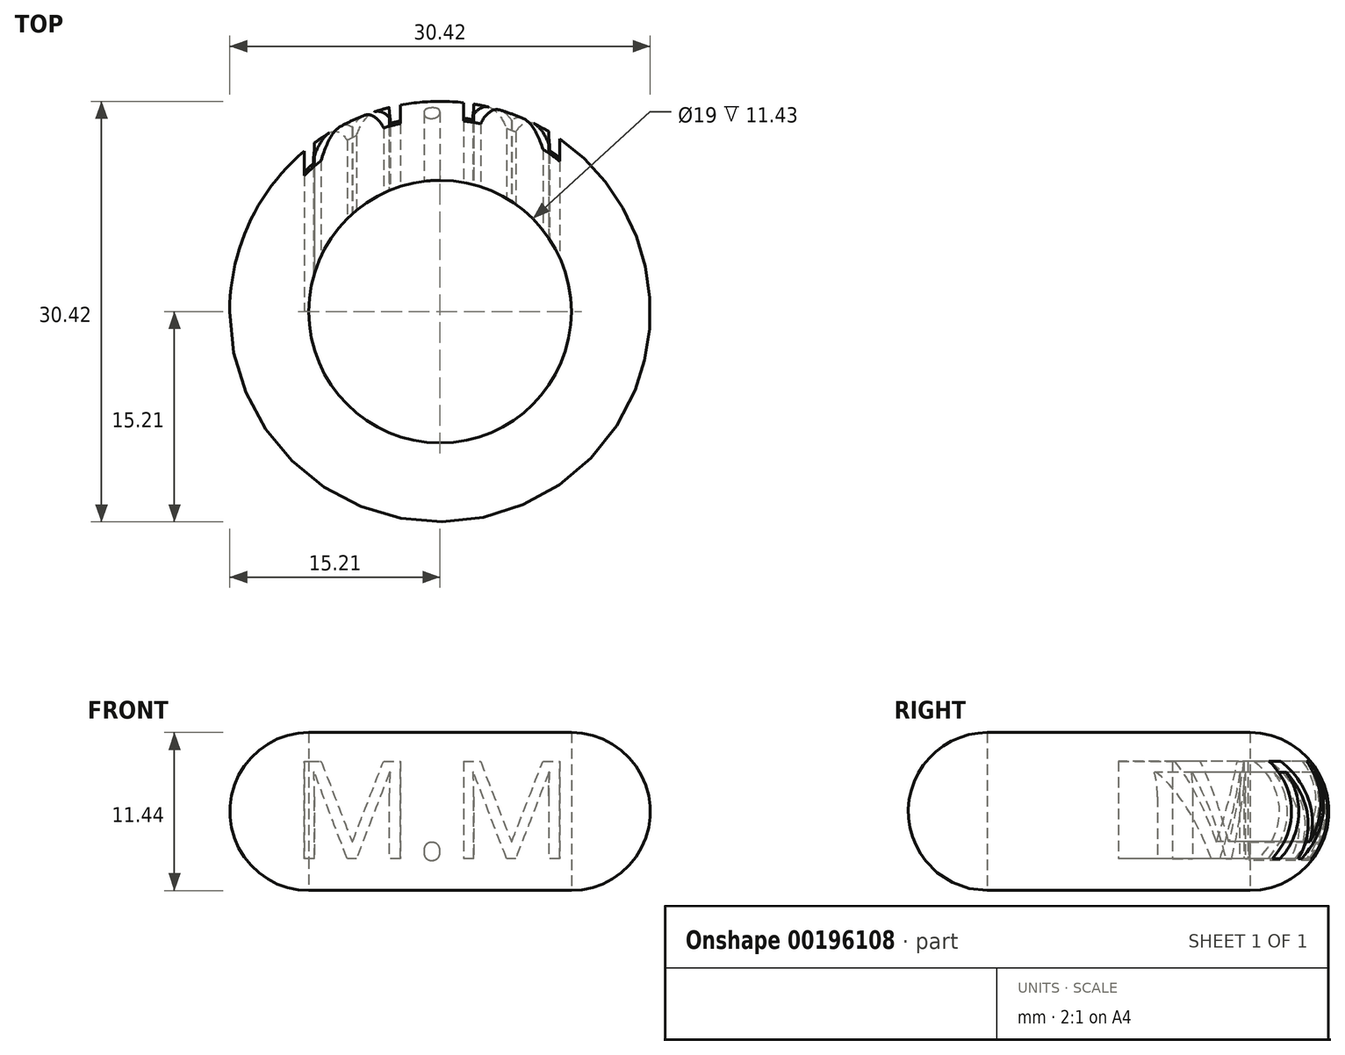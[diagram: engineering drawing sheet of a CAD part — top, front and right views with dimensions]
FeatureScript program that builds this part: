
annotation { "Feature Type Name" : "Feature", "Feature Type Description" : "" }
export const myFeature = defineFeature(function(context is Context, id is Id, definition is map)
    precondition{}
    {
        {
            var Q0;
            Q0=qCreatedBy(makeId("Front.planeOp"),FACE);
            var sketch = newSketch(context, id + "F0", { "sketchPlane" : qUnion([Q0])});
            skArc(sketch, "E0", {"start": v(9.5, -5.72) * mm, "mid": v(15.21, 0) * mm, "end": v(9.5, 5.72) * mm});
            skLineSegment(sketch, "E1", {"start": v(0, 0) * mm, "end": v(0, 10.97) * mm});
            skLineSegment(sketch, "E2", {"start": v(9.5, -5.72) * mm, "end": v(9.5, 5.72) * mm});
            skSolve(sketch);
        }
        {
            var Q0;
            Q0=makeQuery(id+"F0.imprint","IMPRINT",FACE,{"disambiguationData":[TD([[makeQuery(id+"F0.imprint","IMPRINT",EDGE,{"derivedFrom":sQuery(id+"F0.wireOp",EDGE,"E0")}),1.0]])]});
            var Q1;
            Q1=sQuery(id+"F0.wireOp",EDGE,"E1");
            revolve(context, id + "F1", {"entities" : qUnion([Q0]), "axis" : qUnion([Q1]), "revolveType" : RevolveType.FULL});
        }
        {
            var Q0;
            Q0=qCreatedBy(makeId("Front.planeOp"),FACE);
            var sketch = newSketch(context, id + "F2", { "sketchPlane" : qUnion([Q0])});
            skText(sketch, "E3", { "text": "M.M", "fontName": "OpenSans-Regular.ttf"});
            const initialGuessF2  = {"E3": [-0.0108, -0.0034, 1, 0, 0.0071]};
            skSetInitialGuess(sketch, initialGuessF2);
            skSolve(sketch);
        }
        {
            var Q0;
            Q0 = qSketchRegion(id + "F2", true);
            extrude(context, id + "F3", {"entities" : qUnion([Q0]), "operationType" : NewBodyOperationType.REMOVE, "oppositeDirection" : true, "depth" : 25.4 * mm});
        }
    });
